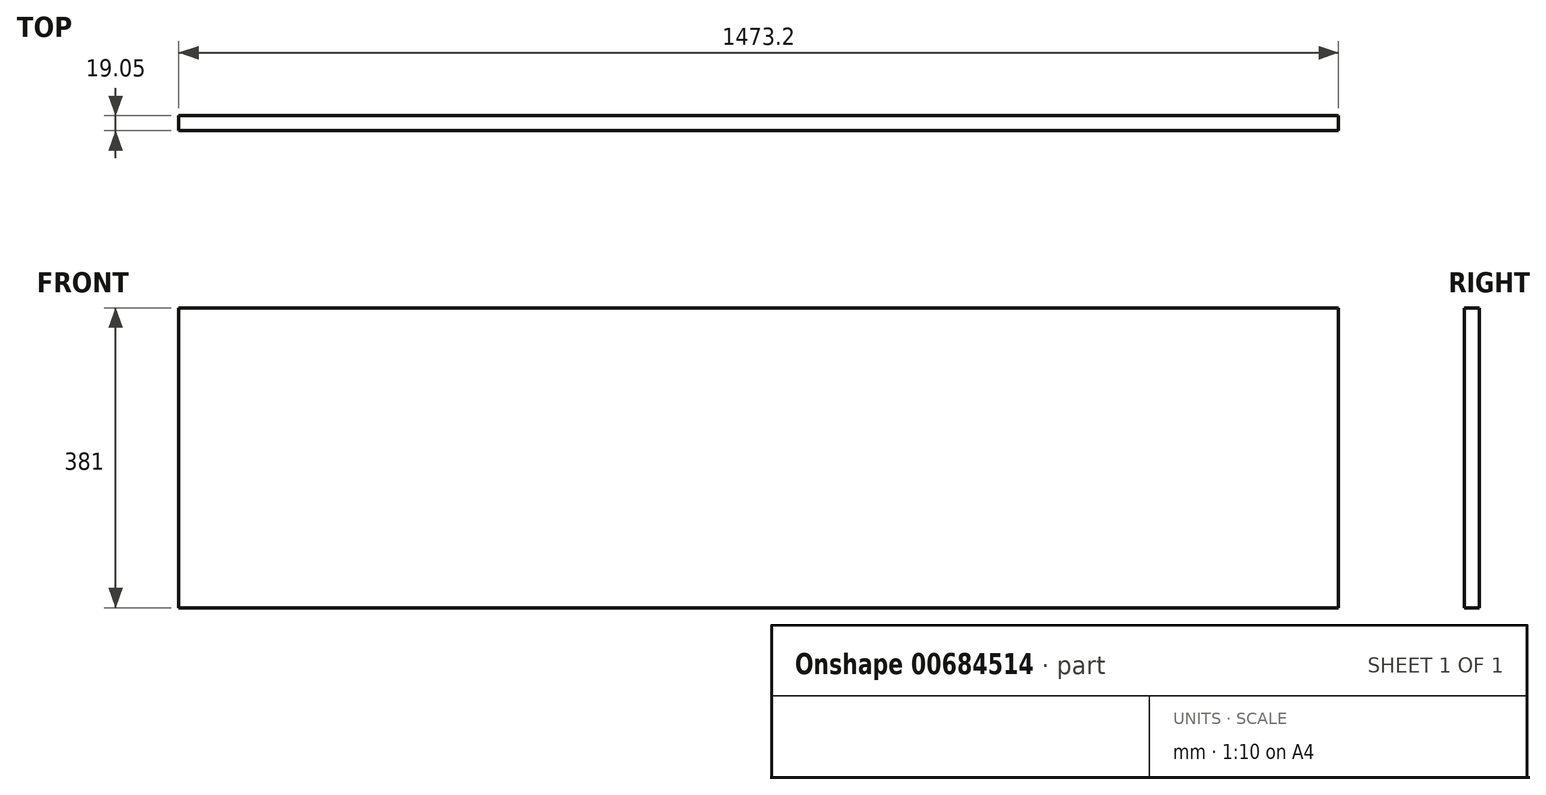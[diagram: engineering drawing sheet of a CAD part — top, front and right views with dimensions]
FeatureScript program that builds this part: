
annotation { "Feature Type Name" : "Feature", "Feature Type Description" : "" }
export const myFeature = defineFeature(function(context is Context, id is Id, definition is map)
    precondition{}
    {
        {
            var Q0;
            Q0=qCreatedBy(makeId("Front.planeOp"),FACE);
            var sketch = newSketch(context, id + "F0", { "sketchPlane" : qUnion([Q0])});
            skLineSegment(sketch, "E0.bottom", {"start": v(-290.57, 219.07) * mm, "end": v(1182.63, 219.07) * mm});
            skLineSegment(sketch, "E0.top", {"start": v(-290.57, -161.93) * mm, "end": v(1182.63, -161.93) * mm});
            skLineSegment(sketch, "E0.left", {"start": v(-290.57, 219.07) * mm, "end": v(-290.57, -161.93) * mm});
            skLineSegment(sketch, "E0.right", {"start": v(1182.63, 219.07) * mm, "end": v(1182.63, -161.93) * mm});
            skSolve(sketch);
        }
        {
            var Q0;
            Q0 = qSketchRegion(id + "F0", true);
            extrude(context, id + "F1", {"entities" : qUnion([Q0]), "depth" : 19.05 * mm, "offsetDistance" : 25.4 * mm});
        }
    });
